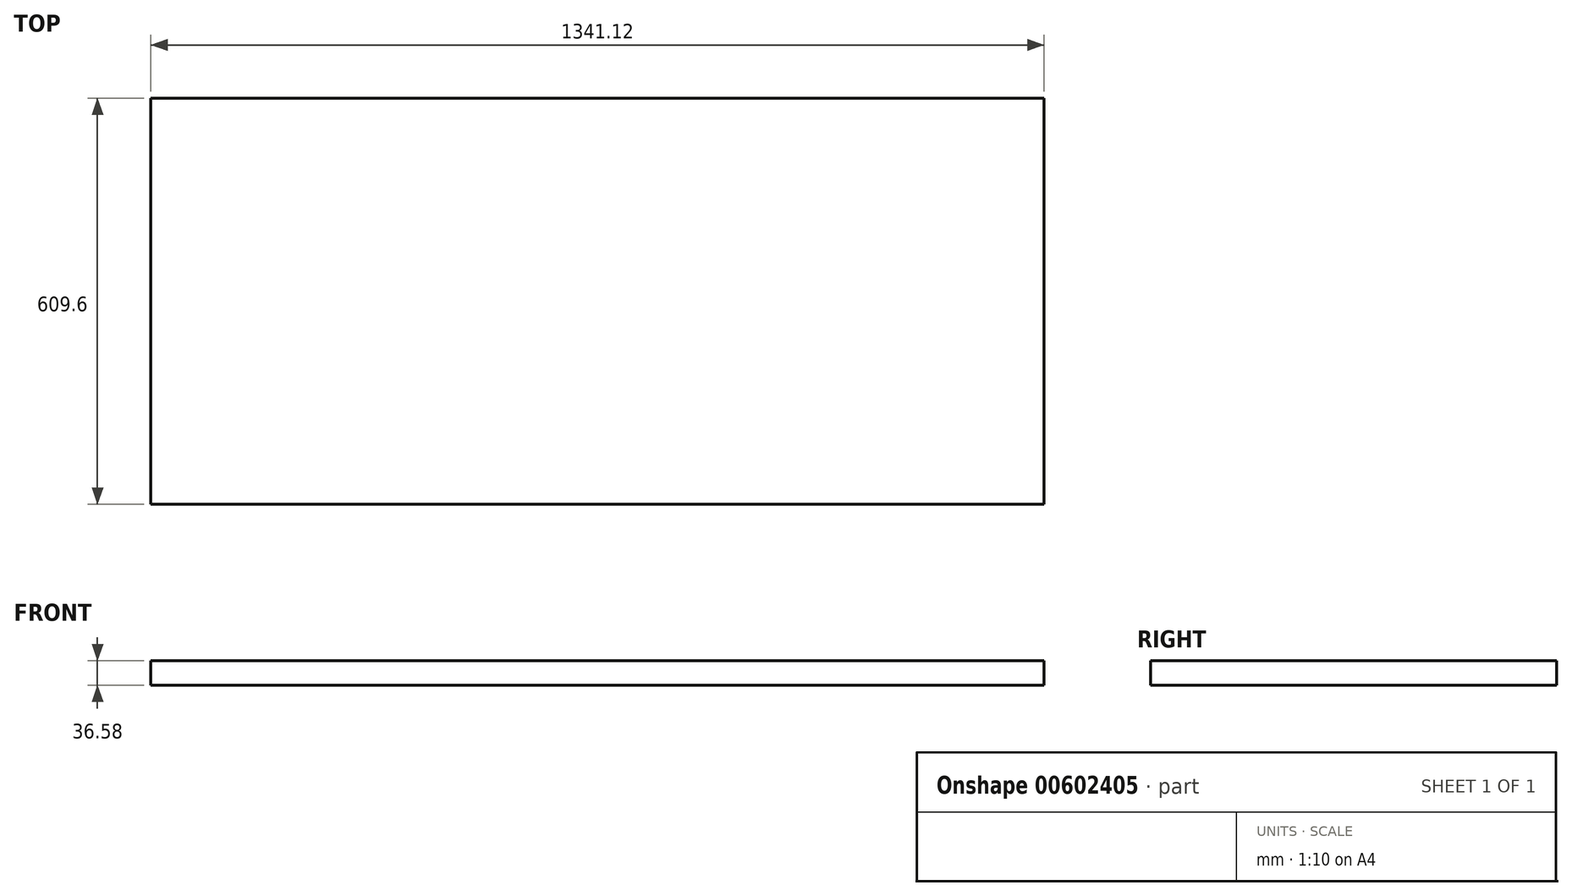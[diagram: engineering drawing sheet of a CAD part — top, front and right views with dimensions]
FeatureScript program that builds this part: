
annotation { "Feature Type Name" : "Feature", "Feature Type Description" : "" }
export const myFeature = defineFeature(function(context is Context, id is Id, definition is map)
    precondition{}
    {
        {
            var Q0;
            Q0=qCreatedBy(makeId("Top.planeOp"),FACE);
            var sketch = newSketch(context, id + "F0", { "sketchPlane" : qUnion([Q0])});
            skLineSegment(sketch, "E0.bottom", {"start": v(0, 0) * mm, "end": v(1341.12, 0) * mm});
            skLineSegment(sketch, "E0.top", {"start": v(0, -609.6) * mm, "end": v(1341.12, -609.6) * mm});
            skLineSegment(sketch, "E0.left", {"start": v(0, 0) * mm, "end": v(0, -609.6) * mm});
            skLineSegment(sketch, "E0.right", {"start": v(1341.12, 0) * mm, "end": v(1341.12, -609.6) * mm});
            skSolve(sketch);
        }
        {
            var Q0;
            Q0=makeQuery(id+"F0.imprint","IMPRINT",FACE,{"disambiguationData":[TD([[makeQuery(id+"F0.imprint","IMPRINT",EDGE,{"derivedFrom":sQuery(id+"F0.wireOp",EDGE,"E0.bottom")}),-1.0]])]});
            extrude(context, id + "F1", {"entities" : qUnion([Q0]), "depth" : 36.58 * mm, "offsetDistance" : 30.48 * mm});
        }
    });
